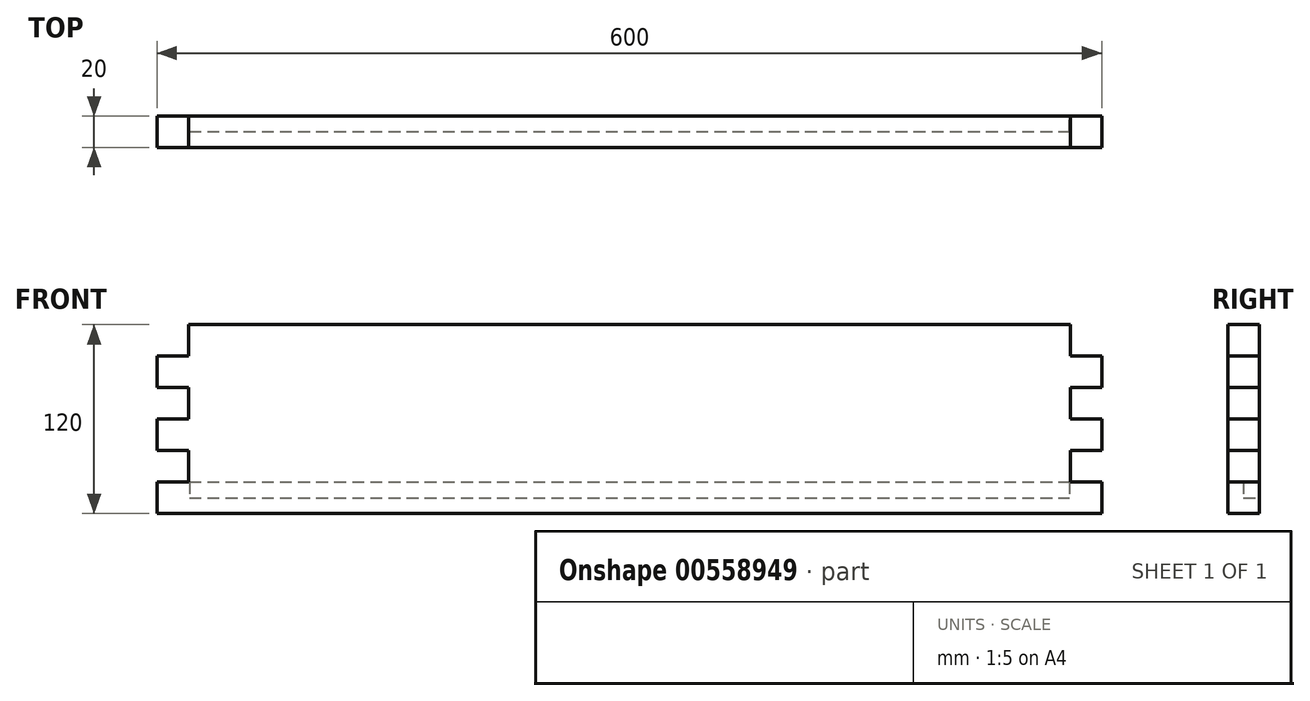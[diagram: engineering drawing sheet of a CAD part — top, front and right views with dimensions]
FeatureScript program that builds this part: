
annotation { "Feature Type Name" : "Feature", "Feature Type Description" : "" }
export const myFeature = defineFeature(function(context is Context, id is Id, definition is map)
    precondition{}
    {
        {
            var Q0;
            Q0=qCreatedBy(makeId("Front.planeOp"),FACE);
            var sketch = newSketch(context, id + "F0", { "sketchPlane" : qUnion([Q0])});
            skLineSegment(sketch, "E0.bottom", {"start": v(300, -60) * mm, "end": v(-300, -60) * mm});
            skLineSegment(sketch, "E0.top", {"start": v(300, 60) * mm, "end": v(-300, 60) * mm});
            skLineSegment(sketch, "E0.left", {"start": v(300, -60) * mm, "end": v(300, 60) * mm});
            skLineSegment(sketch, "E0.right", {"start": v(-300, -60) * mm, "end": v(-300, 60) * mm});
            skPoint(sketch, "E0.middle", {"position": v(0, 0) * mm});
            skSolve(sketch);
        }
        {
            var Q0;
            Q0=makeQuery(id+"F0.imprint","IMPRINT",FACE,{"disambiguationData":[TD([[makeQuery(id+"F0.imprint","IMPRINT",EDGE,{"derivedFrom":sQuery(id+"F0.wireOp",EDGE,"E0.bottom")}),-1.0]])]});
            extrude(context, id + "F1", {"entities" : qUnion([Q0]), "depth" : 20 * mm, "offsetDistance" : 25 * mm});
        }
        {
            var Q0;
            Q0=makeQuery(id+"F1.opExtrude","CAP_FACE",FACE,{"disambiguationData":[OSD([sQuery(id+"F0.wireOp",EDGE,"E0.bottom"),sQuery(id+"F0.wireOp",EDGE,"E0.top"),sQuery(id+"F0.wireOp",EDGE,"E0.left"),sQuery(id+"F0.wireOp",EDGE,"E0.right")])],"isStart":false});
            var sketch = newSketch(context, id + "F2", { "sketchPlane" : qUnion([Q0])});
            skLineSegment(sketch, "E1.bottom", {"start": v(300, -40) * mm, "end": v(280, -40) * mm});
            skLineSegment(sketch, "E1.top", {"start": v(300, -20) * mm, "end": v(280, -20) * mm});
            skLineSegment(sketch, "E1.left", {"start": v(300, -40) * mm, "end": v(300, -20) * mm});
            skLineSegment(sketch, "E1.right", {"start": v(280, -40) * mm, "end": v(280, -20) * mm});
            skLineSegment(sketch, "E2.bottom", {"start": v(300, 0) * mm, "end": v(280, 0) * mm});
            skLineSegment(sketch, "E2.top", {"start": v(300, 20) * mm, "end": v(280, 20) * mm});
            skLineSegment(sketch, "E2.left", {"start": v(300, 0) * mm, "end": v(300, 20) * mm});
            skLineSegment(sketch, "E2.right", {"start": v(280, 0) * mm, "end": v(280, 20) * mm});
            skLineSegment(sketch, "E3.MirrorCS", {"start": v(-280, 0) * mm, "end": v(-280, 20) * mm});
            skLineSegment(sketch, "E4.MirrorCS", {"start": v(-300, 0) * mm, "end": v(-300, 20) * mm});
            skLineSegment(sketch, "E5.MirrorCS", {"start": v(-300, 20) * mm, "end": v(-280, 20) * mm});
            skLineSegment(sketch, "E6.MirrorCS", {"start": v(-300, 0) * mm, "end": v(-280, 0) * mm});
            skLineSegment(sketch, "E7.MirrorCS", {"start": v(-280, -40) * mm, "end": v(-280, -20) * mm});
            skLineSegment(sketch, "E8.MirrorCS", {"start": v(-300, -40) * mm, "end": v(-300, -20) * mm});
            skLineSegment(sketch, "E9.MirrorCS", {"start": v(-300, -40) * mm, "end": v(-280, -40) * mm});
            skLineSegment(sketch, "E10.MirrorCS", {"start": v(-300, -20) * mm, "end": v(-280, -20) * mm});
            skLineSegment(sketch, "E11.bottom", {"start": v(300, 40) * mm, "end": v(280, 40) * mm});
            skLineSegment(sketch, "E11.top", {"start": v(300, 60) * mm, "end": v(280, 60) * mm});
            skLineSegment(sketch, "E11.left", {"start": v(300, 40) * mm, "end": v(300, 60) * mm});
            skLineSegment(sketch, "E11.right", {"start": v(280, 40) * mm, "end": v(280, 60) * mm});
            skLineSegment(sketch, "E12.MirrorCS", {"start": v(-300, 60) * mm, "end": v(-280, 60) * mm});
            skLineSegment(sketch, "E13.MirrorCS", {"start": v(-280, 40) * mm, "end": v(-280, 60) * mm});
            skLineSegment(sketch, "E14.MirrorCS", {"start": v(-300, 40) * mm, "end": v(-300, 60) * mm});
            skLineSegment(sketch, "E15.MirrorCS", {"start": v(-300, 40) * mm, "end": v(-280, 40) * mm});
            skSolve(sketch);
        }
        {
            var Q0;
            Q0 = qSketchRegion(id + "F2", true);
            extrude(context, id + "F3", {"entities" : qUnion([Q0]), "operationType" : NewBodyOperationType.REMOVE, "endBound" : BoundingType.UP_TO_NEXT, "oppositeDirection" : true, "depth" : 25 * mm, "offsetDistance" : 25 * mm});
        }
        {
            var Q0;
            Q0=makeQuery(id+"F1.opExtrude","CAP_FACE",FACE,{"disambiguationData":[OSD([sQuery(id+"F0.wireOp",EDGE,"E0.bottom"),sQuery(id+"F0.wireOp",EDGE,"E0.top"),sQuery(id+"F0.wireOp",EDGE,"E0.left"),sQuery(id+"F0.wireOp",EDGE,"E0.right")])],"isStart":true});
            var sketch = newSketch(context, id + "F4", { "sketchPlane" : qUnion([Q0])});
            skLineSegment(sketch, "E16.bottom", {"start": v(279.5, -40) * mm, "end": v(-279.5, -40) * mm});
            skLineSegment(sketch, "E16.top", {"start": v(279.5, -50) * mm, "end": v(-279.5, -50) * mm});
            skLineSegment(sketch, "E16.left", {"start": v(279.5, -40) * mm, "end": v(279.5, -50) * mm});
            skLineSegment(sketch, "E16.right", {"start": v(-279.5, -40) * mm, "end": v(-279.5, -50) * mm});
            skPoint(sketch, "E16.middle", {"position": v(0, -45) * mm});
            skSolve(sketch);
        }
        {
            var Q0;
            Q0 = qSketchRegion(id + "F4", true);
            extrude(context, id + "F5", {"entities" : qUnion([Q0]), "operationType" : NewBodyOperationType.REMOVE, "oppositeDirection" : true, "depth" : 10 * mm, "offsetDistance" : 25 * mm});
        }
    });
